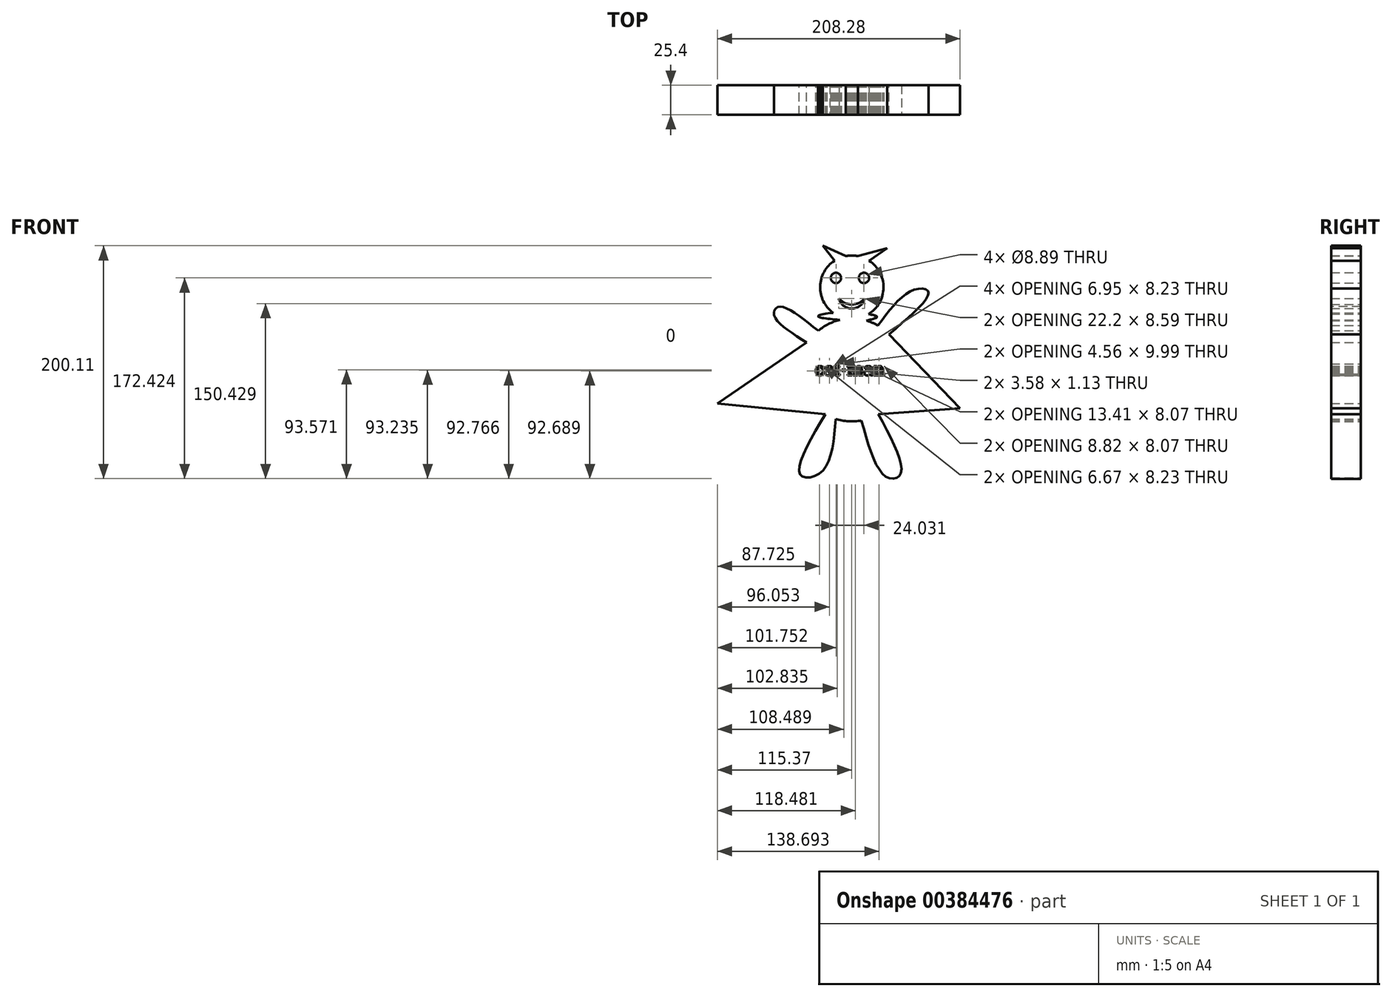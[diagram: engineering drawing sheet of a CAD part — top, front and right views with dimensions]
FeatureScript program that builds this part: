
annotation { "Feature Type Name" : "Feature", "Feature Type Description" : "" }
export const myFeature = defineFeature(function(context is Context, id is Id, definition is map)
    precondition{}
    {
        {
            var Q0;
            Q0=qCreatedBy(makeId("Front.planeOp"),FACE);
            var sketch = newSketch(context, id + "F0", { "sketchPlane" : qUnion([Q0])});
            skArc(sketch, "E0", {"start": v(-14.83, 63.22) * mm, "mid": v(-27.21, 41.12) * mm, "end": v(-16.04, 18.4) * mm});
            skArc(sketch, "E1", {"start": v(-36.79, -55.18) * mm, "mid": v(-30.52, -62.64) * mm, "end": v(-22.77, -68.54) * mm});
            skFitSpline(sketch, "E2", {"points": [v(-36.79, -55.18) * mm, v(-60.96, -58.67) * mm, v(-72.24, -49.53) * mm, v(-51.2, -47.7) * mm, v(-40.92, -47.4) * mm], "startDerivative": vector(-80.95, -29.48) * mm, "endDerivative": vector(40.52, 3.35) * mm});
            skLineSegment(sketch, "E3", {"start": v(-14.83, 63.22) * mm, "end": v(-25, 76.05) * mm});
            skLineSegment(sketch, "E4", {"start": v(-25, 76.05) * mm, "end": v(-5.3, 67.08) * mm});
            skLineSegment(sketch, "E5", {"start": v(14.83, 63.21) * mm, "end": v(30.48, 73.91) * mm});
            skLineSegment(sketch, "E6", {"start": v(30.48, 73.91) * mm, "end": v(5.3, 67.08) * mm});
            skArc(sketch, "E7.trimOffspring", {"start": v(5.3, 67.08) * mm, "mid": v(0, 67.6) * mm, "end": v(-5.3, 67.08) * mm});
            skFitSpline(sketch, "E8", {"points": [v(31.9, 0) * mm, v(65.84, 36.42) * mm, v(52.73, 37.95) * mm, v(22.43, 7.48) * mm], "startDerivative": vector(131.31, 111.56) * mm, "endDerivative": vector(-77.36, -104.57) * mm});
            skFitSpline(sketch, "E9", {"points": [v(-37.84, -7.75) * mm, v(-66.75, 16.61) * mm, v(-62.79, 23.62) * mm, v(-28.75, 2.97) * mm], "startDerivative": vector(-101.33, 63.82) * mm, "endDerivative": vector(98.98, -79.94) * mm});
            skArc(sketch, "E10.trimOffspring", {"start": v(-37.84, -7.75) * mm, "mid": v(-44.09, -27.2) * mm, "end": v(-40.92, -47.4) * mm});
            skArc(sketch, "E11.trimOffspring", {"start": v(22.43, 7.48) * mm, "mid": v(17.66, 9.91) * mm, "end": v(12.63, 11.75) * mm});
            skPoint(sketch, "E12.1.internal.snap0", {"position": v(-44.09, -27.2) * mm});
            skFitSpline(sketch, "E12", {"points": [v(-22.77, -68.54) * mm, v(-44.09, -120.82) * mm, v(-26.33, -118.43) * mm, v(-13.86, -72.63) * mm], "startDerivative": vector(-99.08, -168.97) * mm, "endDerivative": vector(11.95, 152.24) * mm});
            skArc(sketch, "E13.trimOffspring", {"start": v(-13.86, -72.63) * mm, "mid": v(-2.9, -74.76) * mm, "end": v(8.24, -74.08) * mm});
            skFitSpline(sketch, "E14", {"points": [v(22.77, -68.54) * mm, v(41.84, -120.23) * mm, v(29.88, -122.62) * mm, v(8.24, -74.08) * mm], "startDerivative": vector(85.32, -159.12) * mm, "endDerivative": vector(-45.1, 161.32) * mm});
            skArc(sketch, "E15.trimOffspring", {"start": v(22.77, -68.54) * mm, "mid": v(43.84, -36.47) * mm, "end": v(31.9, 0) * mm});
            skCircle(sketch, "E16", {"center": v(-13.62, 48.36) * mm, "radius": 4.45 * mm});
            skCircle(sketch, "E17", {"center": v(10.41, 48.36) * mm, "radius": 4.45 * mm});
            skArc(sketch, "E18", {"start": v(-11.1, 30.66) * mm, "mid": v(0, 22.08) * mm, "end": v(11.1, 30.66) * mm});
            skArc(sketch, "E19", {"start": v(-10.13, 51.12) * mm, "mid": v(-12.73, 47.85) * mm, "end": v(-14.31, 43.97) * mm});
            skArc(sketch, "E20.trimOffspring", {"start": v(-11.1, 30.66) * mm, "mid": v(0, 25.63) * mm, "end": v(11.1, 30.66) * mm});
            skLineSegment(sketch, "E21", {"start": v(-38.8, -7.14) * mm, "end": v(-115.37, -59.5) * mm});
            skLineSegment(sketch, "E22", {"start": v(-115.37, -59.5) * mm, "end": v(-22.77, -68.54) * mm});
            skFitSpline(sketch, "E23", {"points": [v(12.63, 11.75) * mm, v(21.63, 15.22) * mm, v(-16.04, 18.4) * mm, v(-28.84, 15.22) * mm, v(-10.23, 12.4) * mm], "startDerivative": vector(80.05, 19.67) * mm, "endDerivative": vector(106.6, -8.93) * mm});
            skText(sketch, "E24", { "text": "cat-man", "fontName": "RobotoSlab-Regular.ttf"});
            skArc(sketch, "E25.trimOffspring", {"start": v(-10.23, 12.4) * mm, "mid": v(-20.05, 8.78) * mm, "end": v(-28.75, 2.97) * mm});
            skArc(sketch, "E26.trimOffspring", {"start": v(3.78, 13.43) * mm, "mid": v(26.57, 34.49) * mm, "end": v(14.83, 63.21) * mm});
            skLineSegment(sketch, "E27", {"start": v(31.9, 0) * mm, "end": v(92.91, -63.53) * mm});
            skLineSegment(sketch, "E28", {"start": v(92.91, -63.53) * mm, "end": v(22.77, -68.54) * mm});
            const initialGuessF0  = {"E24": [-0.03164, -0.03533, 1, 0, 0.0108]};
            skSetInitialGuess(sketch, initialGuessF0);
            skSolve(sketch);
        }
        {
            var Q0;
            Q0 = qSketchRegion(id + "F0", true);
            extrude(context, id + "F1", {"entities" : qUnion([Q0]), "depth" : 25.4 * mm});
        }
    });
